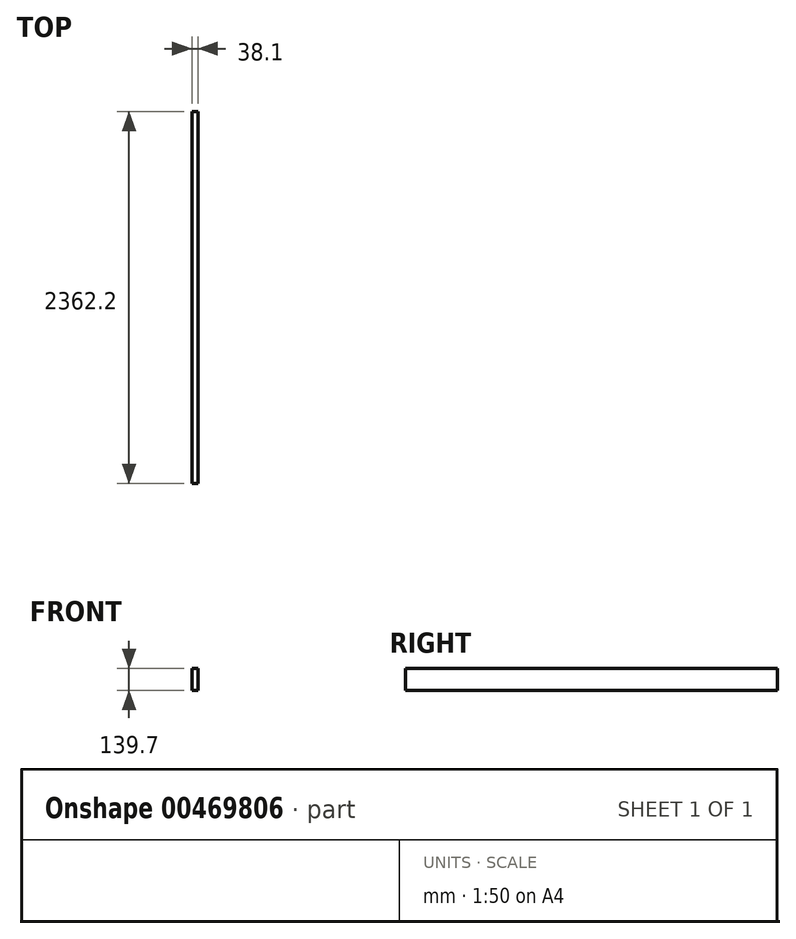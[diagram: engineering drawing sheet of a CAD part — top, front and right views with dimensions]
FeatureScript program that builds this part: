
annotation { "Feature Type Name" : "Feature", "Feature Type Description" : "" }
export const myFeature = defineFeature(function(context is Context, id is Id, definition is map)
    precondition{}
    {
        {
            var Q0;
            Q0=qCreatedBy(makeId("Front.planeOp"),FACE);
            var sketch = newSketch(context, id + "F0", { "sketchPlane" : qUnion([Q0])});
            skLineSegment(sketch, "E0.bottom", {"start": v(19.05, 69.85) * mm, "end": v(-19.05, 69.85) * mm});
            skLineSegment(sketch, "E0.top", {"start": v(19.05, -69.85) * mm, "end": v(-19.05, -69.85) * mm});
            skLineSegment(sketch, "E0.left", {"start": v(19.05, 69.85) * mm, "end": v(19.05, -69.85) * mm});
            skLineSegment(sketch, "E0.right", {"start": v(-19.05, 69.85) * mm, "end": v(-19.05, -69.85) * mm});
            skPoint(sketch, "E0.middle", {"position": v(0, 0) * mm});
            skSolve(sketch);
        }
        {
            var Q0;
            Q0=qSketchRegion(id+"F0",true);
            extrude(context, id + "F1", {"entities" : qUnion([Q0]), "oppositeDirection" : true, "depth" : 2362.2 * mm});
        }
    });
